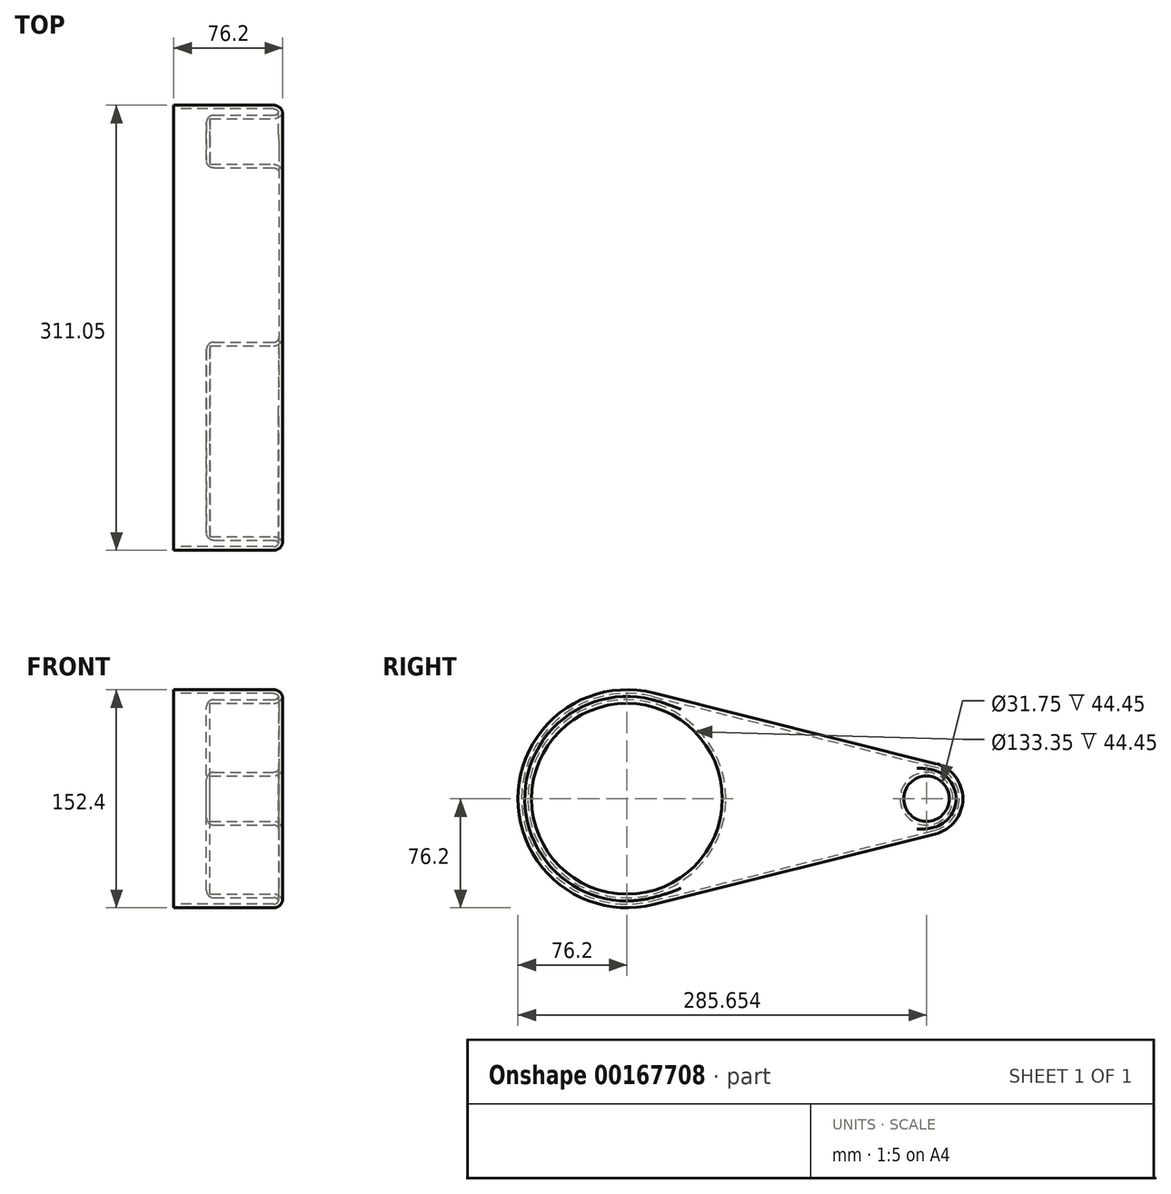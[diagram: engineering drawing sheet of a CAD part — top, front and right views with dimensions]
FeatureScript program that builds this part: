
annotation { "Feature Type Name" : "Feature", "Feature Type Description" : "" }
export const myFeature = defineFeature(function(context is Context, id is Id, definition is map)
    precondition{}
    {
        {
            var Q0;
            Q0=qCreatedBy(makeId("Right.planeOp"),FACE);
            var sketch = newSketch(context, id + "F0", { "sketchPlane" : qUnion([Q0])});
            skCircle(sketch, "E0", {"center": v(0, 0) * mm, "radius": 76.2 * mm});
            skCircle(sketch, "E1", {"center": v(209.45, 0) * mm, "radius": 25.4 * mm});
            skLineSegment(sketch, "E2", {"start": v(18.48, 73.92) * mm, "end": v(215.61, 24.64) * mm});
            skLineSegment(sketch, "E3", {"start": v(18.48, -73.92) * mm, "end": v(215.61, -24.64) * mm});
            skSolve(sketch);
        }
        {
            var Q0;
            {var subQ0=sQuery(id+"F0.wireOp",EDGE,"E2");Q0=makeQuery(id+"F0.imprint","IMPRINT",FACE,{"disambiguationData":[TD([[makeQuery(id+"F0.imprint","IMPRINT",EDGE,{"derivedFrom":subQ0}),-1.0]])]});}
            var Q1;
            {var subQ0=sQuery(id+"F0.wireOp",EDGE,"E1");var subQ1=makeQuery(id+"F0.imprint","INTERSECT",VERTEX,{"derivedFrom":[subQ0,sQuery(id+"F0.wireOp",EDGE,"E2")]});Q1=makeQuery(id+"F0.imprint","IMPRINT",FACE,{"disambiguationData":[TD([[makeQuery(id+"F0.imprint","IMPRINT",EDGE,{"disambiguationData":[TD([[subQ1,-1.0]])],"derivedFrom":subQ0}),1.0]])]});}
            var Q2;
            {var subQ0=sQuery(id+"F0.wireOp",EDGE,"E0");var subQ1=makeQuery(id+"F0.imprint","INTERSECT",VERTEX,{"derivedFrom":[subQ0,sQuery(id+"F0.wireOp",EDGE,"E2")]});Q2=makeQuery(id+"F0.imprint","IMPRINT",FACE,{"disambiguationData":[TD([[makeQuery(id+"F0.imprint","IMPRINT",EDGE,{"disambiguationData":[TD([[subQ1,-1.0]])],"derivedFrom":subQ0}),1.0]])]});}
            extrude(context, id + "F1", {"entities" : qUnion([Q0, Q1, Q2]), "depth" : 76.2 * mm});
        }
        {
            var Q0;
            Q0=makeQuery(id+"F1.opExtrude","CAP_FACE",FACE,{"disambiguationData":[OSD([sQuery(id+"F0.wireOp",EDGE,"E0"),sQuery(id+"F0.wireOp",EDGE,"E1"),sQuery(id+"F0.wireOp",EDGE,"E2"),sQuery(id+"F0.wireOp",EDGE,"E3")])],"isStart":false});
            var sketch = newSketch(context, id + "F2", { "sketchPlane" : qUnion([Q0])});
            skCircle(sketch, "E4", {"center": v(0, 0) * mm, "radius": 66.68 * mm});
            skCircle(sketch, "E5", {"center": v(209.45, 0) * mm, "radius": 15.88 * mm});
            skSolve(sketch);
        }
        {
            var Q0;
            Q0=makeQuery(id+"F2.imprint","IMPRINT",FACE,{"disambiguationData":[TD([[makeQuery(id+"F2.imprint","IMPRINT",EDGE,{"derivedFrom":sQuery(id+"F2.wireOp",EDGE,"E4")}),1.0]])]});
            var Q1;
            Q1=makeQuery(id+"F2.imprint","IMPRINT",FACE,{"disambiguationData":[TD([[makeQuery(id+"F2.imprint","IMPRINT",EDGE,{"derivedFrom":sQuery(id+"F2.wireOp",EDGE,"E5")}),1.0]])]});
            extrude(context, id + "F3", {"entities" : qUnion([Q0, Q1]), "operationType" : NewBodyOperationType.REMOVE, "oppositeDirection" : true, "depth" : 50.8 * mm});
        }
        {
            var Q0;
            Q0=makeQuery(id+"F1.opExtrude","CAP_FACE",FACE,{"disambiguationData":[OSD([sQuery(id+"F0.wireOp",EDGE,"E0"),sQuery(id+"F0.wireOp",EDGE,"E1"),sQuery(id+"F0.wireOp",EDGE,"E2"),sQuery(id+"F0.wireOp",EDGE,"E3")])],"isStart":false});
            var Q1;
            Q1=makeQuery(id+"F3.boolean.opBoolean","COPY",EDGE,{"derivedFrom":makeQuery(id+"F3.opExtrude","CAP_EDGE",EDGE,{"disambiguationData":[OSD([sQuery(id+"F2.wireOp",EDGE,"E4")])],"isStart":true})});
            var Q2;
            Q2=makeQuery(id+"F3.boolean.opBoolean","COPY",EDGE,{"derivedFrom":makeQuery(id+"F3.opExtrude","CAP_EDGE",EDGE,{"disambiguationData":[OSD([sQuery(id+"F2.wireOp",EDGE,"E5")])],"isStart":true})});
            fillet(context, id + "F4", {"entities" : qUnion([Q0, Q1, Q2]), "radius" : 6.35 * mm, "tangentPropagation" : true, "allowEdgeOverflow" : false});
        }
        {
            var Q0;
            Q0=makeQuery(id+"F1.opExtrude","CAP_FACE",FACE,{"disambiguationData":[OSD([sQuery(id+"F0.wireOp",EDGE,"E0"),sQuery(id+"F0.wireOp",EDGE,"E1"),sQuery(id+"F0.wireOp",EDGE,"E2"),sQuery(id+"F0.wireOp",EDGE,"E3")])],"isStart":true});
            shell(context, id + "F5", {"entities" : qUnion([Q0]), "thickness" : 2.54 * mm});
        }
        {
            var Q0;
            {var subQ0=sQuery(id+"F2.wireOp",EDGE,"E5");Q0=makeQuery(id+"F5.opShell","OFFSET_FACE",FACE,{"disambiguationData":[OSD([subQ0]),TDD([makeQuery(id+"F3.boolean.opBoolean","COPY",FACE,{"derivedFrom":makeQuery(id+"F3.opExtrude","CAP_FACE",FACE,{"disambiguationData":[OSD([subQ0])],"isStart":false})})])]});}
            var Q1;
            {var subQ0=sQuery(id+"F2.wireOp",EDGE,"E4");Q1=makeQuery(id+"F5.opShell","OFFSET_FACE",FACE,{"disambiguationData":[OSD([subQ0]),TDD([makeQuery(id+"F3.boolean.opBoolean","COPY",FACE,{"derivedFrom":makeQuery(id+"F3.opExtrude","CAP_FACE",FACE,{"disambiguationData":[OSD([subQ0])],"isStart":false})})])]});}
            fillet(context, id + "F6", {"entities" : qUnion([Q0, Q1]), "radius" : 5.08 * mm, "tangentPropagation" : true, "allowEdgeOverflow" : false});
        }
    });
